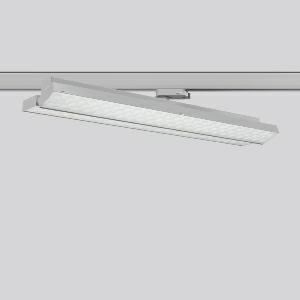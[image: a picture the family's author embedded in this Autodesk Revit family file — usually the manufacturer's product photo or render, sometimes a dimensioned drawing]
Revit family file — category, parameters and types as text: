
# Revit family: tx-move_742161_004_39c3
name_source: partatom
category: Lighting Fixtures
units: mm (PartAtom-declared; Revit-internal decimal feet)

## family parameters
Cut with Voids When Loaded = No
Host = Face
Light Source = No
Part Type = Normal
Room Calculation Point = No
Round Connector Dimension = Use Diameter
Shared = No

## types (1)
- MultiLumen 1 (1 x LED Modul 830, 2900 lm, 3000)
    Apparent Load = 41 VA
    CIE Flux Codes = 90 97 99 100 100
    Color Rendering = 80
    Color Temperature = 3000
    Default Elevation = 1800 mm
    Description = Series: TX-MOVE
Multifunctional surface-mounted spotlight for area lighting. Very flat design. Housing: sheet steel, powder-coated. Rotation range: 356°. Swivel range: 90°. Consistent alignment possible with visible tilt scale. High-efficiency LED units with optimum light control thanks to clear plastic (PC) lens optics. Spezielle Mikrostrukturen reduzieren Gelbsaum. Symmetrical light distribution. With multi adaptor for 3-circuit tracks 230 V. Suitable for Track on ceiling. MultiLumen: Luminous flux adjustable in 3 steps. Factory setting is the highest luminous flux. Environmentally friendly and resource-saving due to replaceable and recyclable components. Very good glare control, ideal for till areas. 
Colour: silver, matt (approx. RAL 9006)
Length: 570 mm
Width: 119 mm
Height: 92 mm
Lamp: LED
Socket: without socket
Colour temperature: 3000K
Colour rendering index (CRI): 80
System power: 41 W
Rated luminous flux: 5800 lm
Luminous efficiency: 141 lm/W
System power 2: 57 W
Rated luminous flux 2: 7850 lm
Luminous efficiency 2: 138 lm/W
System power 3: 73 W
Rated luminous flux 3: 9600 lm
Luminous efficiency 3: 132 lm/W
Control gear: Regulated power supply
Protection class: I
Type of protection: IP 20
    Height = 75 mm
    Lamp = 1 x LED Modul 830
    Lamp Light Flux = 2900 lm
    Lamp count = 1
    Length = 569 mm
    Lifetime = 50000 h
    Luminous efficacy = 141 lm/W
    Manufacturer = RZB
    ModVariant = No
    Model = 742161.004
    Mounting Place = Ceiling
    Mounting Type = Surface mounted
    Number of Poles = 1
    OnlyDefault = Yes
    Power Factor = 1
    Product Name = TX-MOVE
    Product group = Track mounted projectors
    ProductGroupID = 301
    Protection Class = Protection class I
    Protection Degree = IP 20
    RLX_Detail_Level = 1
    RLX_Emergency_Light_Flux = 0 lm
    RLX_Emergency_Type = 0
    RLX_Emergency_Type_DB = No
    RlxData = <blob elided: 33205 chars, md5=d1edd3f6>
    Socket = socket
    Standby Power = 0 W
    System Light Flux = 5800 lm
    System Power = 41 W
    Type Comments = MultiLumen 1
    Type Image = 742162.004.jpg
    URL = http://relux.com
    VarID = multilumen_1
    Voltage = 0 V
    Weight = 0.00 kg
    Width = 119 mm

## geometry (parser evidence)
native form markers: Blend x4, Sweep x16
no freeform markers — native parametric forms only
